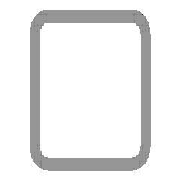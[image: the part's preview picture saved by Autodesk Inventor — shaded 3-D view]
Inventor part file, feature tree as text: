
AUTODESK INVENTOR PART (.ipt)
format: ipt  version: 2025.1 (Build 291241020, 241B)  size: 145,408 bytes
history: native  units: mm (DEFAULTED — no unit token found)
features: other x4, sketch x1, plane x1
ambient origin geometry x8: Origin, YZ Plane, XZ Plane, XY Plane, X Axis, Y Axis, Z Axis, Center Point
bodies: Solid1 (feature_tree), Body (feature_tree)
feature tree (6):
  parser-record x1  (decoder bookkeeping rows leaked as tree rows — omitted from the tree; the rows remain in map.json)
  other  "Driven Length"
  other  "Start plane"
  other  "End plane"
  sketch  "Sketch3"  dims[d3=1150.0mm d4=0.0mm d7=6.0mm d9=100.0mm d11=100.0mm d12=3.0mm d13=50.0mm d14=1200.0mm d15=50.0mm d16=50.0mm d17=90.0deg d18=1150.0mm]
  plane  "Work Plane3"
